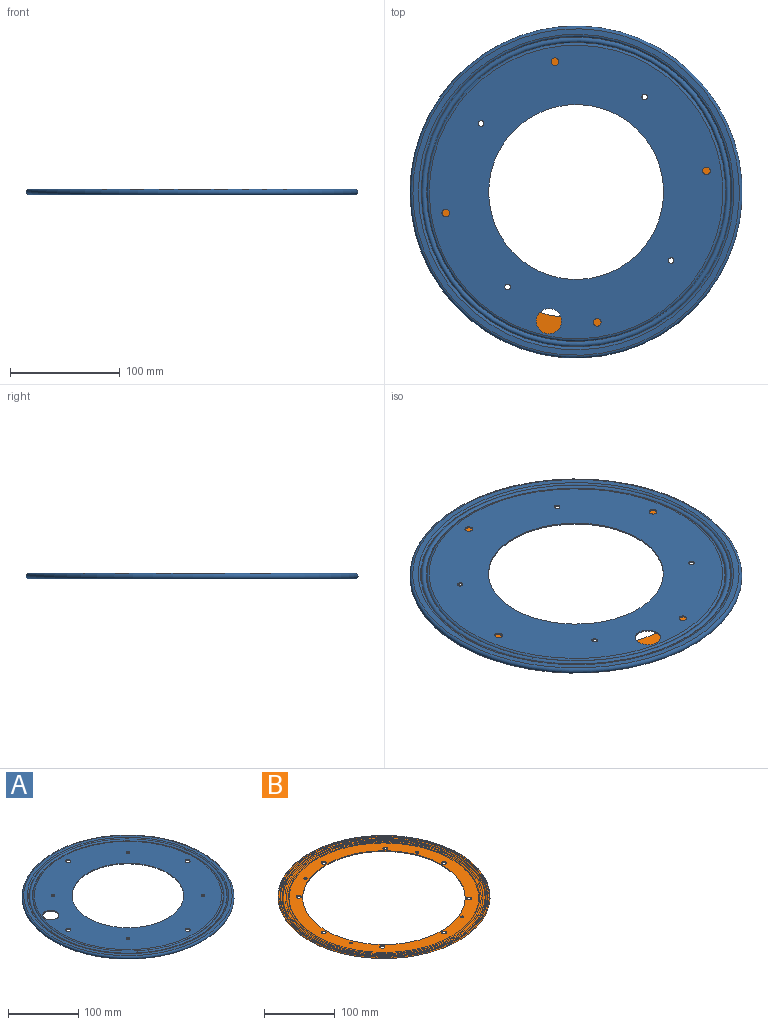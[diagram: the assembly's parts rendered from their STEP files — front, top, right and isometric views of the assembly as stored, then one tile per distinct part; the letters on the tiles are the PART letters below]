
ASSEMBLY  parts=2 mates=1
PART A: 29 faces, bbox 326.9x326.9x5.3 mm
  f0: torus R=140.9mm, axis (0,0,-1), area 2481.1mm2, adj f1,f19
  f1: torus R=138.43mm, axis (0,0,-1), area 2719.8mm2, adj f0,f2
  f2: torus R=135.94mm, axis (0,0,-1), area 2473.9mm2, adj f1,f3
  f3: torus R=133.59mm, axis (0,0,-1), area 1172.2mm2, adj f2,f4
  f4: plane 267.17x267.17mm, normal (0,0,-1), area 35559.4mm2, adj f3,f5,f20,f21,f22,f23,f24,f25
  f5: cylinder r=79.5mm len=159mm, axis (0,0,-1), area 554.3mm2, adj f4,f6
  f6: plane 266.92x266.92mm, normal (0,0,1), area 35454.7mm2, adj f5,f7,f20,f21,f22,f23,f24,f25
  f7: torus R=133.42mm, axis (0,0,-1), area 2236.6mm2, adj f6,f8
  f8: torus R=135.96mm, axis (0,0,-1), area 710.3mm2, adj f7,f9
  f9: torus R=138.43mm, axis (0,0,-1), area 4458.2mm2, adj f8,f10
  f10: torus R=140.9mm, axis (0,0,-1), area 736.1mm2, adj f9,f11
  f11: torus R=143.4mm, axis (0,0,-1), area 2321.8mm2, adj f10,f12
  f12: plane 296.8x296.8mm, normal (0,0,1), area 4583.6mm2, adj f11,f13
  f13: torus R=148.4mm, axis (0,0,-1), area 7701.1mm2, adj f12,f14
  f14: plane 296.8x296.8mm, normal (0,0,-1), area 2677.6mm2, adj f13,f15
  f15: cylinder r=145.5mm len=291mm, axis (0,0,-1), area 896.5mm2, adj f14,f16
  f16: plane 296.8x296.8mm, normal (0,0,1), area 2677.6mm2, adj f15,f17
  f17: torus R=148.4mm, axis (0,0,-1), area 4776.6mm2, adj f16,f18
  f18: plane 296.8x296.8mm, normal (0,0,-1), area 4629mm2, adj f17,f19
  f19: torus R=143.26mm, axis (0,0,-1), area 1414.9mm2, adj f0,f18
  f20: cylinder r=11.5mm len=23mm, axis (0,0,1), area 80.2mm2, adj f4,f6
  f21: cylinder r=3.5mm len=7mm, axis (0,0,-1), area 24.4mm2, adj f4,f6
  f22: cylinder r=3.5mm len=7mm, axis (0,0,-1), area 24.4mm2, adj f4,f6
  f23: cylinder r=3.5mm len=7mm, axis (0,0,-1), area 24.4mm2, adj f4,f6
  f24: cylinder r=3.5mm len=7mm, axis (0,0,-1), area 24.4mm2, adj f4,f6
  f25: cylinder r=2.5mm len=5mm, axis (0,0,1), area 17.4mm2, adj f4,f6
  f26: cylinder r=2.5mm len=5mm, axis (0,0,1), area 17.4mm2, adj f4,f6
  f27: cylinder r=2.5mm len=5mm, axis (0,0,1), area 17.4mm2, adj f4,f6
  f28: cylinder r=2.5mm len=5mm, axis (0,0,1), area 17.4mm2, adj f4,f6
PART B: 35 faces, bbox 323.4x323.4x3.4 mm
  f0: torus R=133.43mm, axis (0,0,-1), area 2197.7mm2, adj f1,f22
  f1: plane 266.86x266.86mm, normal (0,0,-1), area 14372.1mm2, adj f0,f2,f23,f24,f25,f26,f27,f28
  f2: cylinder r=114.5mm len=229mm, axis (0,0,-1), area 878.4mm2, adj f1,f3
  f3: plane 267.34x267.34mm, normal (0,0,1), area 14573.3mm2, adj f2,f4,f23,f24,f25,f26,f27,f28
  f4: torus R=133.67mm, axis (0,0,-1), area 1126.8mm2, adj f3,f5
  f5: torus R=135.93mm, axis (0,0,-1), area 2360.1mm2, adj f4,f6
  f6: torus R=138.43mm, axis (0,0,-1), area 2819.2mm2, adj f5,f7
  f7: torus R=140.92mm, axis (0,0,-1), area 2564.2mm2, adj f6,f8
  f8: torus R=143.32mm, axis (0,0,-1), area 1415.5mm2, adj f7,f9
  f9: torus R=143.42mm, axis (0,0,-1), area 562.7mm2, adj f8,f10
  f10: torus R=145.52mm, axis (0,0,-1), area 1873.3mm2, adj f9,f11
  f11: plane 293.25x293.25mm, normal (0,0,1), area 1016.2mm2, adj f10,f12
  f12: cylinder r=146.63mm len=293.25mm, axis (0,0,-1), area 921.3mm2, adj f11,f13
  f13: plane 296.8x296.8mm, normal (0,0,1), area 1643.9mm2, adj f12,f14
  f14: torus R=148.4mm, axis (0,0,-1), area 2941.9mm2, adj f13,f15
  f15: plane 296.8x296.8mm, normal (0,0,-1), area 2660.4mm2, adj f14,f16
  f16: torus R=145.52mm, axis (0,0,-1), area 806mm2, adj f15,f17
  f17: torus R=143.42mm, axis (0,0,-1), area 1615.7mm2, adj f16,f18
  f18: torus R=143.43mm, axis (0,0,-1), area 2322.2mm2, adj f17,f19
  f19: torus R=140.92mm, axis (0,0,-1), area 382.7mm2, adj f18,f20
  f20: torus R=140.92mm, axis (0,0,-1), area 367.6mm2, adj f19,f21
  f21: torus R=138.43mm, axis (0,0,-1), area 4505.6mm2, adj f20,f22
  f22: torus R=135.93mm, axis (0,0,-1), area 710.1mm2, adj f0,f21
  f23: cylinder r=3.5mm len=7mm, axis (0,0,-1), area 26.9mm2, adj f1,f3
  f24: cylinder r=3.5mm len=7mm, axis (0,0,-1), area 26.9mm2, adj f1,f3
  f25: cylinder r=3.5mm len=7mm, axis (0,0,-1), area 26.9mm2, adj f1,f3
  f26: cylinder r=3.5mm len=7mm, axis (0,0,-1), area 26.9mm2, adj f1,f3
  f27: cylinder r=2.25mm len=4.5mm, axis (0,0,-1), area 17.3mm2, adj f1,f3
  f28: cylinder r=2.25mm len=4.5mm, axis (0,0,-1), area 17.3mm2, adj f1,f3
  f29: cylinder r=2.25mm len=4.5mm, axis (0,0,-1), area 17.3mm2, adj f1,f3
  f30: cylinder r=2.25mm len=4.5mm, axis (0,0,-1), area 17.3mm2, adj f1,f3
  f31: cylinder r=3.5mm len=7mm, axis (0,0,-1), area 26.9mm2, adj f1,f3
  f32: cylinder r=3.5mm len=7mm, axis (0,0,-1), area 26.9mm2, adj f1,f3
  f33: cylinder r=3.5mm len=7mm, axis (0,0,-1), area 26.9mm2, adj f1,f3
  f34: cylinder r=3.5mm len=7mm, axis (0,0,-1), area 26.9mm2, adj f1,f3
PLACE A rot(axis=(0,0,1),99.2deg) t=(-15,-4.6,2.86)mm
PLACE B t=(-15,-4.6,2.92)mm fixed
MATE revolute B.f0 <-> A.f0  axis (0,0,-1) through (-15,-4.6,3.15)mm
